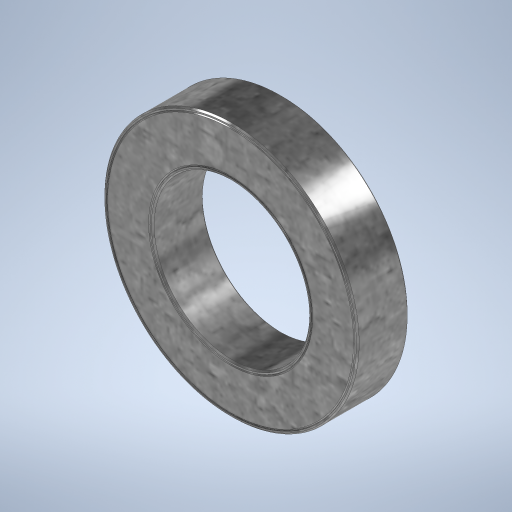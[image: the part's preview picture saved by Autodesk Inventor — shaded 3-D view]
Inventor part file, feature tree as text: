
AUTODESK INVENTOR PART (.ipt)
format: ipt  version: 2023 (Build 270158000, 158)  size: 403,968 bytes
history: native  units: mm
features: sketch x2, other x1, extrude x1, chamfer x1, revolve x1
ambient origin geometry x8: Origin, YZ Plane, XZ Plane, XY Plane, X Axis, Y Axis, Z Axis, Center Point
bodies: Body1 (feature_tree)
feature tree (6):
  other  "솔리드1"
  extrude  "돌출1"  Depth=55.0mm
  chamfer  "모따기1"  Distance=90.0mm
  revolve  "회전1"
  sketch  "스케치1"
  sketch  "스케치2"
